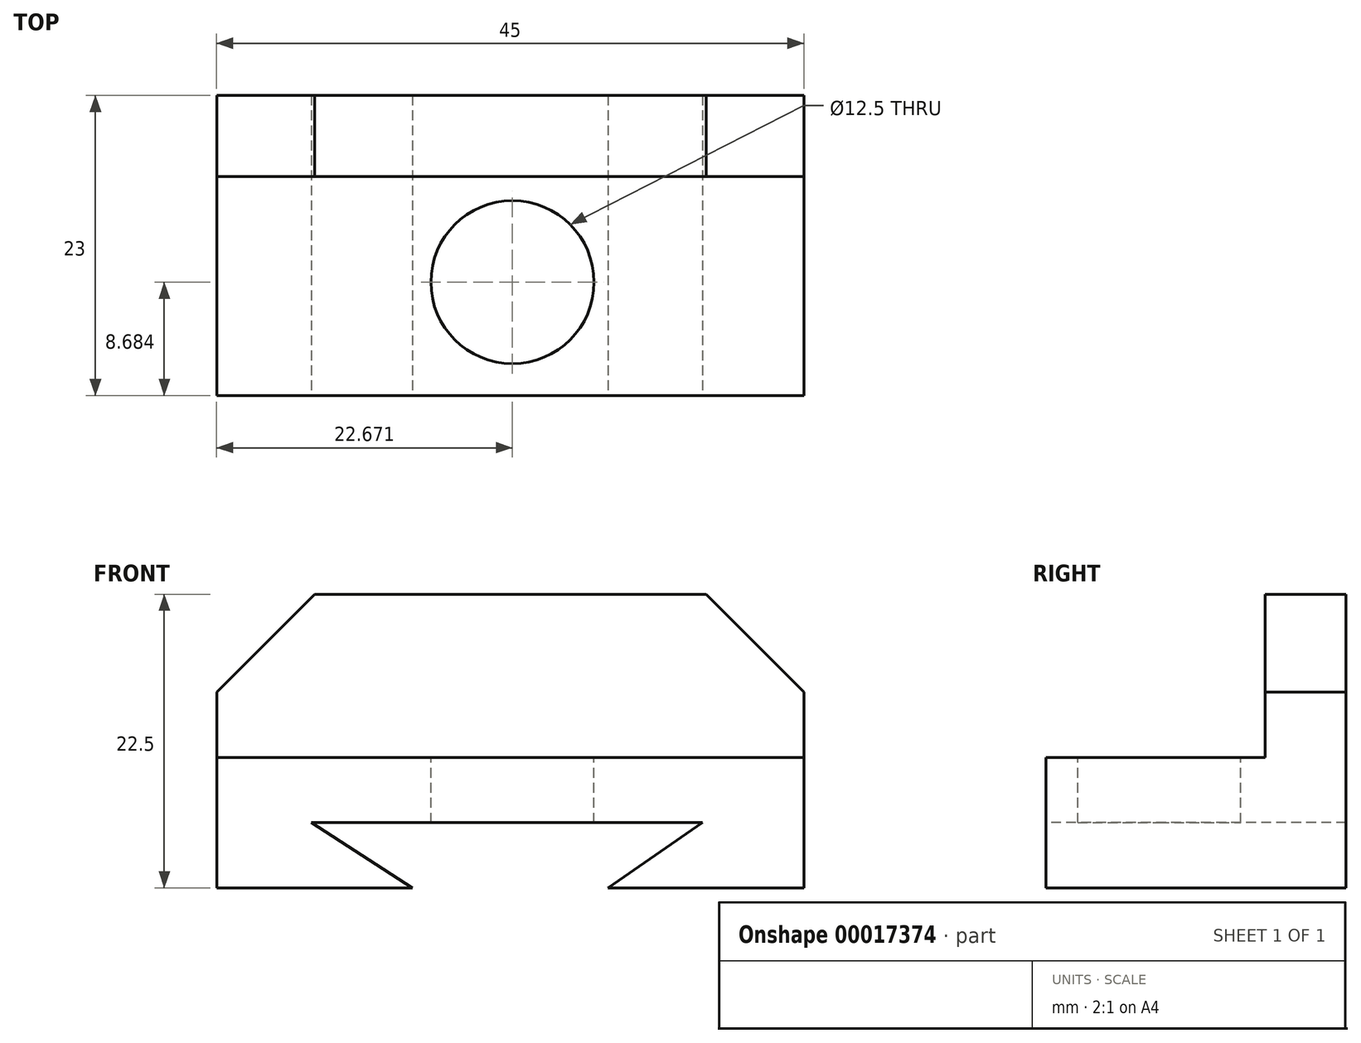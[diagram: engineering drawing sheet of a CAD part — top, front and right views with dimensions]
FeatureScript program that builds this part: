
annotation { "Feature Type Name" : "Feature", "Feature Type Description" : "" }
export const myFeature = defineFeature(function(context is Context, id is Id, definition is map)
    precondition{}
    {
        {
            var Q0;
            Q0=qCreatedBy(makeId("Front.planeOp"),FACE);
            var sketch = newSketch(context, id + "F0", { "sketchPlane" : qUnion([Q0])});
            skLineSegment(sketch, "E0", {"start": v(-8.88, 9.8) * mm, "end": v(-8.88, -0.2) * mm});
            skLineSegment(sketch, "E1", {"start": v(-8.88, -0.2) * mm, "end": v(6.12, -0.2) * mm});
            skLineSegment(sketch, "E2", {"start": v(-8.88, 9.8) * mm, "end": v(36.12, 9.8) * mm});
            skLineSegment(sketch, "E3", {"start": v(36.12, 9.8) * mm, "end": v(36.12, -0.2) * mm});
            skLineSegment(sketch, "E4", {"start": v(36.12, -0.2) * mm, "end": v(21.12, -0.2) * mm});
            skPoint(sketch, "E5", {"position": v(-8.88, 4.8) * mm});
            skLineSegment(sketch, "E6", {"start": v(6.12, -0.2) * mm, "end": v(-1.63, 4.8) * mm});
            skPoint(sketch, "E7", {"position": v(36.12, 4.8) * mm});
            skLineSegment(sketch, "E8", {"start": v(21.12, -0.2) * mm, "end": v(28.35, 4.8) * mm});
            skLineSegment(sketch, "E9", {"start": v(28.35, 4.8) * mm, "end": v(-1.63, 4.8) * mm});
            skSolve(sketch);
        }
        {
            var Q0;
            Q0=makeQuery(id+"F0.imprint","IMPRINT",FACE,{"disambiguationData":[TD([[makeQuery(id+"F0.imprint","IMPRINT",EDGE,{"derivedFrom":sQuery(id+"F0.wireOp",EDGE,"E0")}),1.0]])]});
            extrude(context, id + "F1", {"entities" : qUnion([Q0]), "oppositeDirection" : true, "depth" : 23 * mm});
        }
        {
            var Q0;
            Q0=makeQuery(id+"F1.opExtrude","SWEPT_FACE",FACE,{"disambiguationData":[OSD([sQuery(id+"F0.wireOp",EDGE,"E2")])]});
            var sketch = newSketch(context, id + "F2", { "sketchPlane" : qUnion([Q0])});
            skLineSegment(sketch, "E10.bottom", {"start": v(-8.88, 23) * mm, "end": v(36.12, 23) * mm});
            skLineSegment(sketch, "E10.top", {"start": v(-8.88, 16.8) * mm, "end": v(36.12, 16.8) * mm});
            skLineSegment(sketch, "E10.left", {"start": v(-8.88, 23) * mm, "end": v(-8.88, 16.8) * mm});
            skLineSegment(sketch, "E10.right", {"start": v(36.12, 23) * mm, "end": v(36.12, 16.8) * mm});
            skSolve(sketch);
        }
        {
            var Q0;
            Q0=makeQuery(id+"F2.imprint","IMPRINT",FACE,{"disambiguationData":[TD([[makeQuery(id+"F2.imprint","IMPRINT",EDGE,{"derivedFrom":sQuery(id+"F2.wireOp",EDGE,"E10.bottom")}),-1.0]])]});
            extrude(context, id + "F3", {"entities" : qUnion([Q0]), "operationType" : NewBodyOperationType.ADD, "depth" : 12.5 * mm});
        }
        {
            var Q0;
            Q0=makeQuery(id+"F3.opExtrude","SWEPT_FACE",FACE,{"disambiguationData":[OSD([sQuery(id+"F2.wireOp",EDGE,"E10.top")])]});
            var sketch = newSketch(context, id + "F4", { "sketchPlane" : qUnion([Q0])});
            skLineSegment(sketch, "E11", {"start": v(-8.88, 9.8) * mm, "end": v(-8.88, 14.8) * mm});
            skLineSegment(sketch, "E12", {"start": v(-8.88, 22.3) * mm, "end": v(-1.38, 22.3) * mm});
            skLineSegment(sketch, "E13", {"start": v(-8.88, 14.8) * mm, "end": v(-1.38, 22.3) * mm});
            skLineSegment(sketch, "E14", {"start": v(-8.88, 22.3) * mm, "end": v(-8.88, 14.8) * mm});
            skLineSegment(sketch, "E15", {"start": v(36.12, 14.8) * mm, "end": v(36.12, 9.8) * mm});
            skLineSegment(sketch, "E16", {"start": v(36.12, 22.3) * mm, "end": v(28.62, 22.3) * mm});
            skLineSegment(sketch, "E17", {"start": v(36.12, 14.8) * mm, "end": v(28.62, 22.3) * mm});
            skLineSegment(sketch, "E18", {"start": v(36.12, 14.8) * mm, "end": v(36.12, 22.3) * mm});
            skSolve(sketch);
        }
        {
            var Q0;
            Q0=makeQuery(id+"F4.imprint","IMPRINT",FACE,{"disambiguationData":[TD([[makeQuery(id+"F4.imprint","IMPRINT",EDGE,{"derivedFrom":sQuery(id+"F4.wireOp",EDGE,"E12")}),-1.0]])]});
            extrude(context, id + "F5", {"entities" : qUnion([Q0]), "operationType" : NewBodyOperationType.REMOVE, "oppositeDirection" : true, "depth" : 25 * mm});
        }
        {
            var Q0;
            Q0=makeQuery(id+"F4.imprint","IMPRINT",FACE,{"disambiguationData":[TD([[makeQuery(id+"F4.imprint","IMPRINT",EDGE,{"derivedFrom":sQuery(id+"F4.wireOp",EDGE,"E16")}),-1.0]])]});
            extrude(context, id + "F6", {"entities" : qUnion([Q0]), "operationType" : NewBodyOperationType.REMOVE, "oppositeDirection" : true, "depth" : 25 * mm});
        }
        {
            var Q0;
            Q0=makeQuery(id+"F1.opExtrude","SWEPT_FACE",FACE,{"disambiguationData":[OSD([sQuery(id+"F0.wireOp",EDGE,"E2")])]});
            var sketch = newSketch(context, id + "F7", { "sketchPlane" : qUnion([Q0])});
            skCircle(sketch, "E19", {"center": v(13.8, 8.68) * mm, "radius": 6.25 * mm});
            skSolve(sketch);
        }
        {
            var Q0;
            Q0=makeQuery(id+"F7.imprint","IMPRINT",FACE,{"disambiguationData":[TD([[makeQuery(id+"F7.imprint","IMPRINT",EDGE,{"derivedFrom":sQuery(id+"F7.wireOp",EDGE,"E19")}),1.0]])]});
            extrude(context, id + "F8", {"entities" : qUnion([Q0]), "operationType" : NewBodyOperationType.REMOVE, "oppositeDirection" : true, "depth" : 25 * mm});
        }
    });
